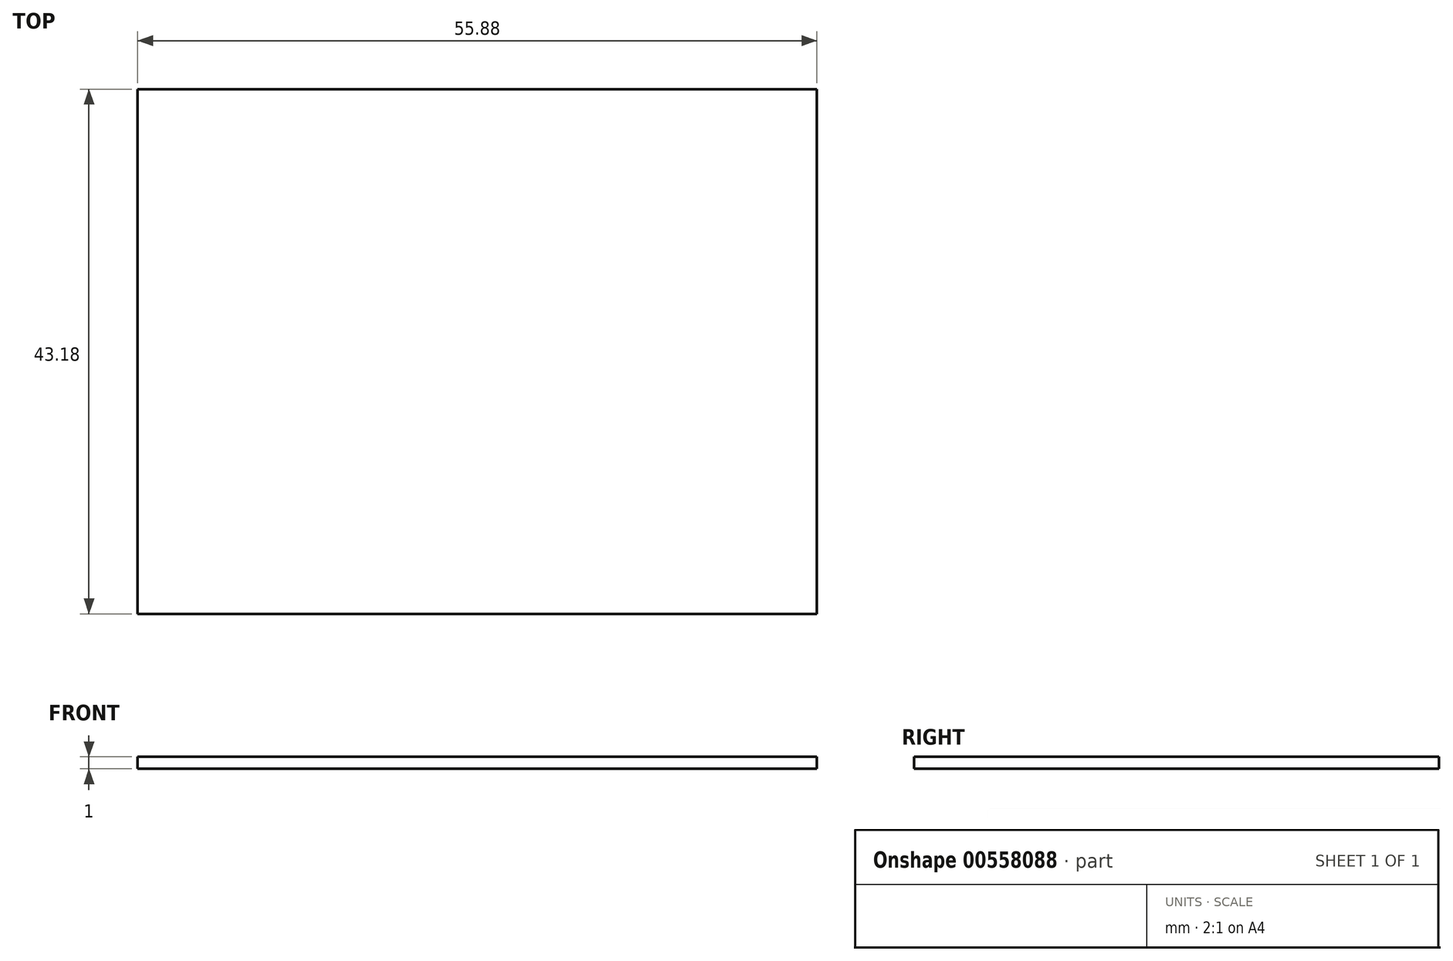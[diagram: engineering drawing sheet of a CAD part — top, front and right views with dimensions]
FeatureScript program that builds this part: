
annotation { "Feature Type Name" : "Feature", "Feature Type Description" : "" }
export const myFeature = defineFeature(function(context is Context, id is Id, definition is map)
    precondition{}
    {
        {
            var Q0;
            Q0=qCreatedBy(makeId("Top.planeOp"),FACE);
            var sketch = newSketch(context, id + "F0", { "sketchPlane" : qUnion([Q0])});
            skLineSegment(sketch, "E0.bottom", {"start": v(-27.94, 21.59) * mm, "end": v(27.94, 21.6) * mm});
            skLineSegment(sketch, "E0.top", {"start": v(-27.94, -21.6) * mm, "end": v(27.94, -21.59) * mm});
            skLineSegment(sketch, "E0.left", {"start": v(-27.94, 21.59) * mm, "end": v(-27.94, -21.6) * mm});
            skLineSegment(sketch, "E0.right", {"start": v(27.94, 21.6) * mm, "end": v(27.94, -21.59) * mm});
            skSolve(sketch);
        }
        {
            var Q0;
            Q0=makeQuery(id+"F0.imprint","IMPRINT",FACE,{"disambiguationData":[TD([[makeQuery(id+"F0.imprint","IMPRINT",EDGE,{"derivedFrom":sQuery(id+"F0.wireOp",EDGE,"E0.bottom")}),-1.0]])]});
            extrude(context, id + "F1", {"entities" : qUnion([Q0]), "depth" : 1 * mm, "offsetDistance" : 25 * mm});
        }
    });
